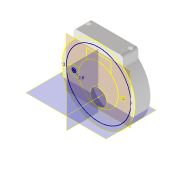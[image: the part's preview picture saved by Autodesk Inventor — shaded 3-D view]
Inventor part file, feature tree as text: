
AUTODESK INVENTOR PART (.ipt)
format: ipt  version: 2022.5 (Build 265521000, 521)  size: 258,048 bytes
history: native  units: mm
features: reference x17, sketch x8, other x7, plane x4, extrude x4, projected_geometry x4, hole x2, revolve x1
ambient origin geometry x8: Origin, YZ Plane, XZ Plane, XY Plane, X Axis, Y Axis, Z Axis, Center Point
bodies: Volumenkörper1 (feature_tree)
feature tree (47):
  plane  "Arbeitsebene1"
  extrude  "Extrusion1"  Depth=2.8mm
  sketch  "Skizze2"  dims[d2=2.8mm d3=12.0mm]
  plane  "Arbeitsebene2"
  extrude  "Extrusion3"  Depth=12.0mm
  plane  "Arbeitsebene4"
  revolve  "Umdrehung1"
  extrude  "Extrusion5"  Depth=3.0mm
  hole  "Bohrung1"  [1 undecoded]
  extrude  "Extrusion6"  Depth=0.872665mm
  hole  "Bohrung2"  [1 undecoded]
  sketch  "Skizze1"  dims[d0=52.0mm d1=2.8mm]
  reference  "Referenz1"
  reference  "Referenz2"
  reference  "Referenz3"
  reference  "Referenz4"
  projected_geometry  "Projizierte Kontur1"
  reference  "Referenz5"
  reference  "Referenz6"
  reference  "Referenz7"
  reference  "Referenz8"
  reference  "Referenz9"
  reference  "Referenz10"
  reference  "Referenz11"
  reference  "Referenz12"
  sketch  "Skizze3"  dims[d4=1.0mm d5=0.0mm d6=3.0mm]
  plane  "Arbeitsebene3"
  other  "Arbeitsachse1"
  sketch  "Skizze4"  dims[d9=2.8mm d10=36.0mm]
  projected_geometry  "Projizierte Kontur2"
  sketch  "Skizze7"  dims[d11=0.872665mm d12=0.872665mm]
  projected_geometry  "Projizierte Kontur3"
  sketch  "Skizze8"  dims[d13=10.0mm d14=0.0mm d15=90.0deg]
  projected_geometry  "Projizierte Kontur4"
  sketch  "Skizze9"  dims[d16=2.8mm]
  reference  "Referenz13"
  reference  "Referenz14"
  reference  "Referenz15"
  sketch  "Skizze10"  dims[d17=0.0mm d18=180.0deg d28=2.0mm d29=3.0mm d30=4.0mm d31=4.0mm d32=0.0mm d33=0.0mm d34=3.0mm d35=6.0mm d36=4.0mm d37=2.0mm d38=90.0deg d39=8.0mm d40=20.594885mm d41=10.0mm d42=0.0mm d43=25.0mm d44=2.8mm d45=6.0mm d46=4.0mm d47=2.0mm d48=90.0deg d49=8.0mm d50=20.594885mm]
  reference  "Referenz16"
  reference  "Referenz17"
  other  "Planktoscope_Mini_Peristalticpump_new.iam"
  other  "00_Stepper_Motor_28BYJ-48:1"
  other  "Pump_Base_Motor_new:1"
  other  "Assembly_Matchboxscope_injectionmolded_xiao:1"
  other  "IM_Matchboxscope_plate:1"
  other  "IM_Matchboxscope_base_xiao_lid:1"
note: 2 required parameter values undecoded (feature->parameter linkage not recoverable at this tier; creation-order binding heuristic only, values carry confidence <= 0.55)
